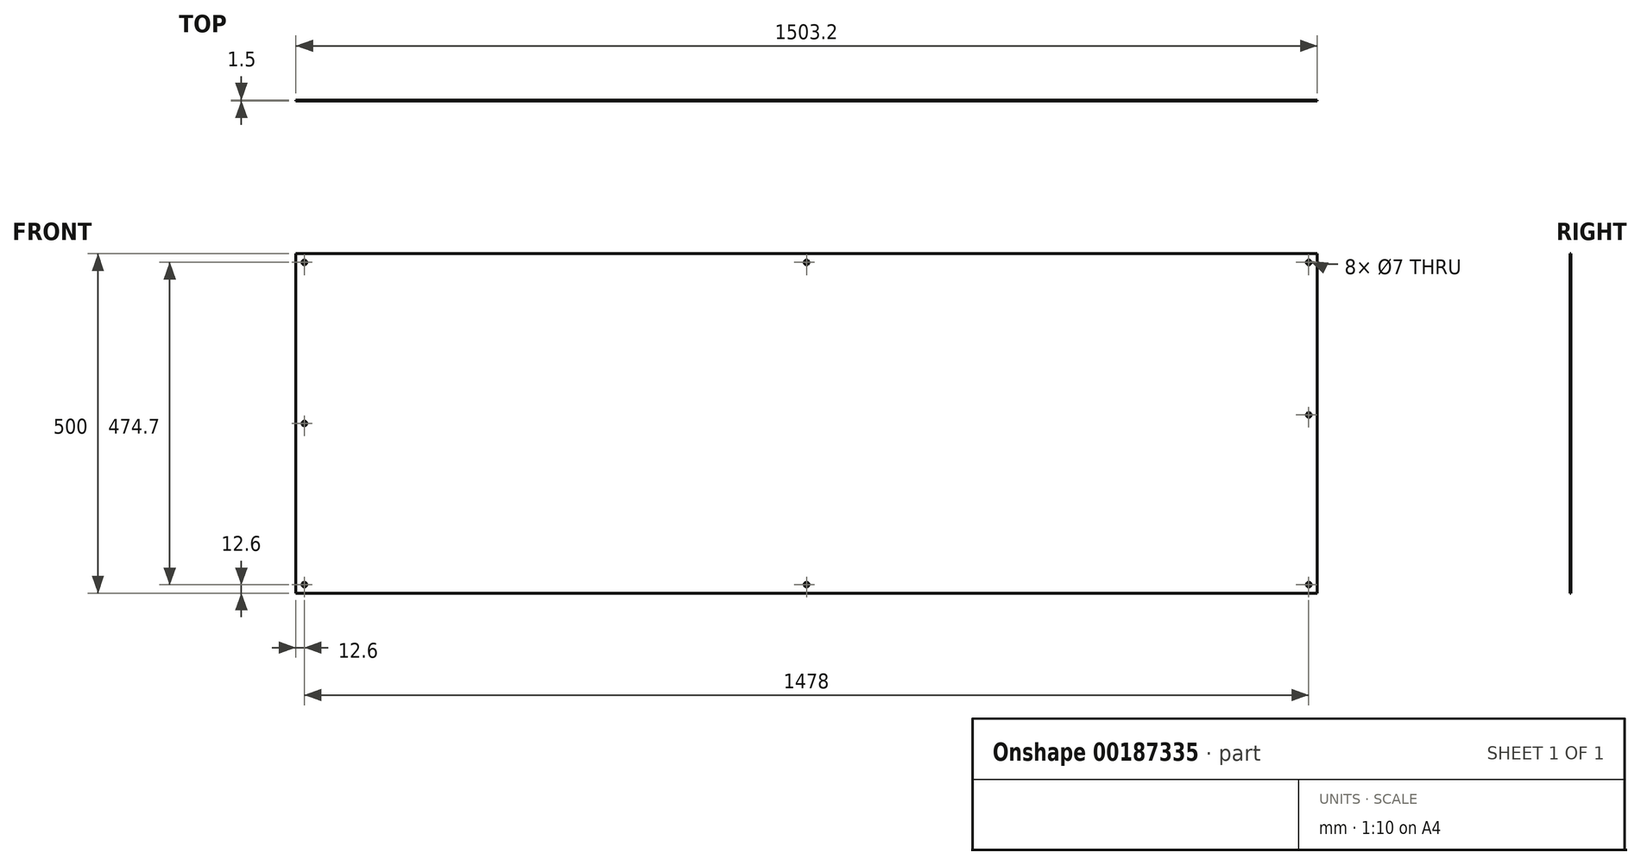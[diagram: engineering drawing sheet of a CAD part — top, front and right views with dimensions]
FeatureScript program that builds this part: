
annotation { "Feature Type Name" : "Feature", "Feature Type Description" : "" }
export const myFeature = defineFeature(function(context is Context, id is Id, definition is map)
    precondition{}
    {
        {
            var Q0;
            Q0=qCreatedBy(makeId("Front.planeOp"),FACE);
            var sketch = newSketch(context, id + "F0", { "sketchPlane" : qUnion([Q0])});
            skLineSegment(sketch, "E0.bottom", {"start": v(751.6, -250) * mm, "end": v(-751.6, -250) * mm});
            skLineSegment(sketch, "E0.top", {"start": v(751.6, 250) * mm, "end": v(-751.6, 250) * mm});
            skLineSegment(sketch, "E0.left", {"start": v(751.6, -250) * mm, "end": v(751.6, 250) * mm});
            skLineSegment(sketch, "E0.right", {"start": v(-751.6, -250) * mm, "end": v(-751.6, 250) * mm});
            skPoint(sketch, "E0.middle", {"position": v(0, 0) * mm});
            skCircle(sketch, "E1", {"center": v(-739, 237.3) * mm, "radius": 3.5 * mm});
            skCircle(sketch, "E2", {"center": v(739, 237.3) * mm, "radius": 3.5 * mm});
            skCircle(sketch, "E3", {"center": v(-739, -237.3) * mm, "radius": 3.5 * mm});
            skCircle(sketch, "E4", {"center": v(739, -237.4) * mm, "radius": 3.5 * mm});
            skCircle(sketch, "E5", {"center": v(739, 12.6) * mm, "radius": 3.5 * mm});
            skCircle(sketch, "E6", {"center": v(-739, 0) * mm, "radius": 3.5 * mm});
            skCircle(sketch, "E7", {"center": v(0, -237.3) * mm, "radius": 3.5 * mm});
            skCircle(sketch, "E8", {"center": v(0, 237.3) * mm, "radius": 3.5 * mm});
            skSolve(sketch);
        }
        {
            var Q0;
            Q0=qSketchRegion(id+"F0",true);
            extrude(context, id + "F1", {"entities" : qUnion([Q0]), "depth" : 1.5 * mm});
        }
    });
